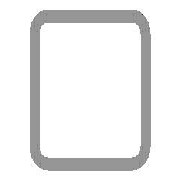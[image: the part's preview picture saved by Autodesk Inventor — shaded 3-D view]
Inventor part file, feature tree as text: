
AUTODESK INVENTOR PART (.ipt)
format: ipt  version: 2025 (Build 290162010, 162A)  size: 133,120 bytes
history: native  units: mm (DEFAULTED — no unit token found)
features: other x4, sketch x1, plane x1
ambient origin geometry x8: Origin, YZ Plane, XZ Plane, XY Plane, X Axis, Y Axis, Z Axis, Center Point
bodies: Solid1 (feature_tree), Body (feature_tree)
feature tree (6):
  parser-record x1  (decoder bookkeeping rows leaked as tree rows — omitted from the tree; the rows remain in map.json)
  other  "Driven Length"
  other  "Start Plane"
  other  "End Plane"
  sketch  "Sketch3"  dims[d3=938.0mm d4=0.0mm d7=4.0mm d9=40.0mm d11=40.0mm d12=2.0mm d13=-0.0mm d14=938.0mm d15=20.0mm d16=20.0mm d17=90.0deg d18=938.0mm]
  plane  "Work Plane3"
